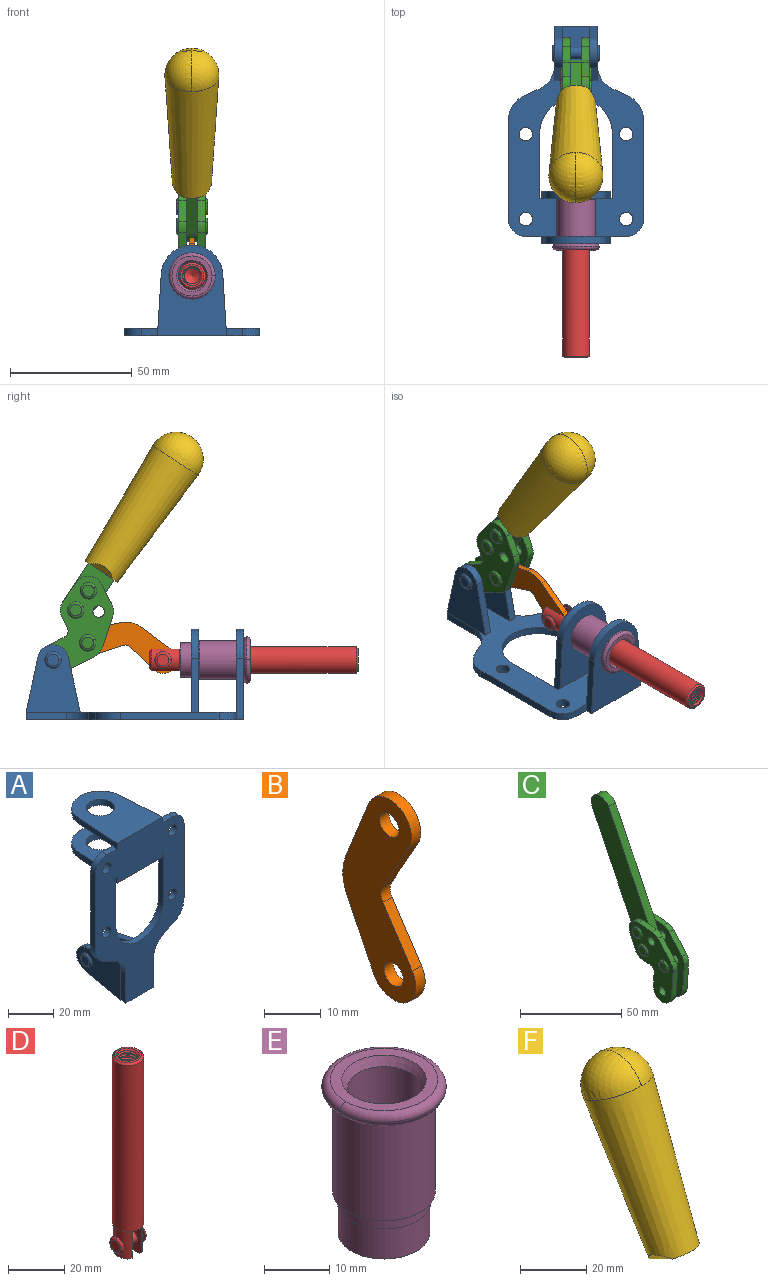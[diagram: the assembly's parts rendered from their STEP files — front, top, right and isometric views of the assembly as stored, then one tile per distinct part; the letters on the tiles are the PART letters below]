
ASSEMBLY  parts=6 mates=6
PART A: 55 faces, bbox 55.7x37.4x89.8 mm
  f0: torus R=2.41mm, axis (-1,0,0), area 15mm2, adj f11,f15,f25
  f1: torus R=2.41mm, axis (-1,0,0), area 15mm2, adj f10,f12,f22
  f2: cylinder r=2.78mm len=5.56mm, axis (0,-1,0), area 54.2mm2, adj f30,f54
  f3: cylinder r=14.99mm len=29.97mm, axis (0,-1,0), area 145.9mm2, adj f30,f49,f53,f54
  f4: cylinder r=2.78mm len=5.56mm, axis (0,-1,0), area 54.2mm2, adj f30,f54
  f5: cylinder r=2.78mm len=5.56mm, axis (0,-1,0), area 54.2mm2, adj f30,f54
  f6: cylinder r=2.78mm len=5.56mm, axis (0,-1,0), area 54.2mm2, adj f30,f54
  f7: cylinder r=6.35mm len=12.7mm, axis (0,0,1), area 123.6mm2, adj f27,f51
  f8: cylinder r=6.35mm len=12.7mm, axis (0,0,-1), area 124.7mm2, adj f21,f35
  f9: cylinder r=2.41mm len=11.18mm, axis (-1,0,0), area 169.4mm2, adj f16,f19
  f10: plane 4.83x4.83mm, normal (1,0,0), area 18.3mm2, adj f1,f12
  f11: plane 4.83x4.83mm, normal (-1,0,0), area 18.3mm2, adj f0,f15
  f12: torus R=2.41mm, axis (-1,0,0), area 15mm2, adj f1,f10,f22
  f13: cylinder r=6.35mm len=12.41mm, axis (1,0,0), area 53.4mm2, adj f18,f19,f22,f23
  f14: cylinder r=6.35mm len=12.41mm, axis (-1,0,0), area 53.4mm2, adj f16,f17,f24,f25
  f15: torus R=2.41mm, axis (-1,0,0), area 15mm2, adj f0,f11,f25
  f16: plane 27.86x22.35mm, normal (1,0,0), area 425.4mm2, adj f9,f14,f17,f24,f30
  f17: plane 22.86x4.97mm, normal (0,0.21,0.98), area 72.5mm2, adj f14,f16,f25,f30
  f18: plane 22.86x4.97mm, normal (0,0.21,0.98), area 72.5mm2, adj f13,f19,f22,f30
  f19: plane 27.86x22.35mm, normal (-1,0,0), area 425.4mm2, adj f9,f13,f18,f23,f30
  f20: cylinder r=12.7mm len=25.35mm, axis (0,0,-1), area 119.8mm2, adj f21,f34,f35,f36
  f21: plane 34.21x28.07mm, normal (0,0,-1), area 702.4mm2, adj f8,f20,f30,f34,f36
  f22: plane 27.96x22.45mm, normal (1,0,0), area 407.2mm2, adj f1,f12,f13,f18,f23,f30,f42,f43
  f23: plane 22.86x4.97mm, normal (0,0.21,-0.98), area 72.5mm2, adj f13,f19,f22,f44
  f24: plane 22.86x4.97mm, normal (0,0.21,-0.98), area 72.5mm2, adj f14,f16,f25,f44
  f25: plane 27.86x22.35mm, normal (-1,0,0), area 407.1mm2, adj f0,f14,f15,f17,f24,f30,f45,f46
  f26: plane 3.1x0.95mm, normal (0,0,-1), area 2.7mm2, adj f30,f49,f50,f54
  f27: plane 34.21x28.07mm, normal (0,0,1), area 702.4mm2, adj f7,f28,f30,f50,f52
  f28: cylinder r=12.7mm len=25.35mm, axis (0,0,1), area 118.8mm2, adj f27,f50,f51,f52
  f29: plane 3.1x0.95mm, normal (0,0,-1), area 2.7mm2, adj f30,f52,f53,f54
  f30: plane 86.54x55.63mm, normal (0,1,0), area 2362.9mm2, adj f2,f3,f4,f5,f6,f16,f17,f18
  f31: plane 40.56x3.1mm, normal (-1,0,0), area 125.7mm2, adj f30,f32,f48,f54
  f32: cylinder r=7.11mm len=7.11mm, axis (0,-1,0), area 34.6mm2, adj f30,f31,f33,f54
  f33: plane 6.67x3.1mm, normal (0,0,1), area 20.4mm2, adj f30,f32,f34,f54
  f34: plane 25.39x3.13mm, normal (-1,0.06,0), area 79.5mm2, adj f20,f21,f33,f35,f54
  f35: plane 37.31x28.45mm, normal (0,0,1), area 789.9mm2, adj f8,f20,f34,f36,f54
  f36: plane 25.39x3.13mm, normal (1,0.06,0), area 79.5mm2, adj f20,f21,f35,f37,f54
  f37: plane 6.67x3.1mm, normal (0,0,1), area 20.4mm2, adj f30,f36,f38,f54
  f38: cylinder r=7.11mm len=7.11mm, axis (0,-1,0), area 34.6mm2, adj f30,f37,f39,f54
  f39: plane 40.56x3.1mm, normal (1,0,0), area 125.7mm2, adj f30,f38,f40,f54
  f40: cylinder r=11.18mm len=10.16mm, axis (0,-1,0), area 39.5mm2, adj f30,f39,f41,f54
  f41: plane 6.09x3.1mm, normal (0.42,0,-0.91), area 20.8mm2, adj f30,f40,f42,f54
  f42: cylinder r=11.18mm len=9.41mm, axis (0,-1,0), area 37.2mm2, adj f22,f30,f41,f43,f54
  f43: plane 16.5x3.1mm, normal (1,0,0), area 51.1mm2, adj f22,f42,f44,f54
  f44: plane 17.37x3.1mm, normal (0,0,-1), area 53.8mm2, adj f23,f24,f30,f43,f45,f54
  f45: plane 16.5x3.1mm, normal (-1,0,0), area 51.1mm2, adj f25,f44,f46,f54
  f46: cylinder r=11.18mm len=9.41mm, axis (0,-1,0), area 37.2mm2, adj f25,f30,f45,f47,f54
  f47: plane 6.09x3.1mm, normal (-0.42,0,-0.91), area 20.8mm2, adj f30,f46,f48,f54
  f48: cylinder r=11.18mm len=10.16mm, axis (0,-1,0), area 39.5mm2, adj f30,f31,f47,f54
  f49: plane 26.54x3.1mm, normal (-1,0,0), area 82.3mm2, adj f3,f26,f30,f54
  f50: plane 25.39x3.1mm, normal (1,0.06,0), area 78.8mm2, adj f26,f27,f28,f51,f54
  f51: plane 37.31x28.45mm, normal (0,0,-1), area 789.9mm2, adj f7,f28,f50,f52,f54
  f52: plane 25.39x3.1mm, normal (-1,0.06,0), area 78.8mm2, adj f27,f28,f29,f51,f54
  f53: plane 26.54x3.1mm, normal (1,0,0), area 82.3mm2, adj f3,f29,f30,f54
  f54: plane 89.66x55.63mm, normal (0,-1,0), area 2678.5mm2, adj f2,f3,f4,f5,f6,f26,f29,f31
PART B: 12 faces, bbox 2.3x18.2x42.8 mm
  f0: cylinder r=2.4mm len=4.8mm, axis (1,0,0), area 34.9mm2, adj f4,f11
  f1: cylinder r=10.41mm len=8.47mm, axis (1,0,0), area 20.2mm2, adj f4,f9,f10,f11
  f2: cylinder r=3.05mm len=3.16mm, axis (1,0,0), area 7.7mm2, adj f4,f6,f7,f11
  f3: cylinder r=2.4mm len=4.8mm, axis (1,0,0), area 34.9mm2, adj f4,f11
  f4: plane 42.81x18.23mm, normal (-1,0,0), area 414.1mm2, adj f0,f1,f2,f3,f5,f6,f7,f8
  f5: cylinder r=5.54mm len=10.67mm, axis (1,0,0), area 41.8mm2, adj f4,f6,f10,f11
  f6: plane 11.66x6.53mm, normal (0,-0.87,-0.49), area 30.9mm2, adj f2,f4,f5,f11
  f7: plane 11.17x7.33mm, normal (0,-0.84,0.55), area 30.9mm2, adj f2,f4,f8,f11
  f8: cylinder r=5.54mm len=10.51mm, axis (1,0,0), area 41.8mm2, adj f4,f7,f9,f11
  f9: plane 13.67x6.67mm, normal (0,0.9,-0.44), area 35.1mm2, adj f1,f4,f8,f11
  f10: plane 14.1x5.7mm, normal (0,0.93,0.37), area 35.1mm2, adj f1,f4,f5,f11
  f11: plane 42.81x18.23mm, normal (1,0,0), area 414.1mm2, adj f0,f1,f2,f3,f5,f6,f7,f8
PART C: 59 faces, bbox 12.9x60.2x99.6 mm
  f0: torus R=2.39mm, axis (-1,0,0), area 14.9mm2, adj f20,f43,f51
  f1: torus R=2.39mm, axis (-1,0,0), area 14.9mm2, adj f19,f42,f51
  f2: torus R=2.39mm, axis (-1,0,0), area 14.9mm2, adj f18,f35,f51
  f3: torus R=2.39mm, axis (-1,0,0), area 14.9mm2, adj f14,f17,f23
  f4: torus R=2.39mm, axis (-1,0,0), area 14.9mm2, adj f13,f16,f23
  f5: torus R=2.39mm, axis (-1,0,0), area 14.9mm2, adj f12,f15,f23
  f6: cylinder r=2.39mm len=4.78mm, axis (1,0,0), area 46.5mm2, adj f48,f50,f51
  f7: cylinder r=2.39mm len=4.78mm, axis (1,0,0), area 46.5mm2, adj f50,f51
  f8: cylinder r=6.35mm len=12.68mm, axis (1,0,0), area 61.8mm2, adj f38,f39,f50,f51
  f9: cylinder r=2.39mm len=4.78mm, axis (-1,0,0), area 70.5mm2, adj f46,f50
  f10: cylinder r=2.39mm len=4.78mm, axis (-1,0,0), area 46.5mm2, adj f23,f45,f46
  f11: cylinder r=2.39mm len=4.78mm, axis (-1,0,0), area 46.5mm2, adj f23,f46
  f12: plane 4.78x4.78mm, normal (1,0,0), area 17.9mm2, adj f5,f15
  f13: plane 4.78x4.78mm, normal (1,0,0), area 17.9mm2, adj f4,f16
  f14: plane 4.78x4.78mm, normal (1,0,0), area 17.9mm2, adj f3,f17
  f15: torus R=2.39mm, axis (-1,0,0), area 14.9mm2, adj f5,f12,f23
  f16: torus R=2.39mm, axis (-1,0,0), area 14.9mm2, adj f4,f13,f23
  f17: torus R=2.39mm, axis (-1,0,0), area 14.9mm2, adj f3,f14,f23
  f18: plane 4.78x4.78mm, normal (-1,0,0), area 17.9mm2, adj f2,f35
  f19: plane 4.78x4.78mm, normal (-1,0,0), area 17.9mm2, adj f1,f42
  f20: plane 4.78x4.78mm, normal (-1,0,0), area 17.9mm2, adj f0,f43
  f21: plane 2.26x0.2mm, normal (1,0,0), area 0.2mm2, adj f31,f44
  f22: plane 2.26x0.2mm, normal (-1,0,0), area 0.2mm2, adj f41,f44
  f23: plane 39.37x30.77mm, normal (1,0,0), area 565.5mm2, adj f3,f4,f5,f10,f11,f15,f16,f17
  f24: cylinder r=6.1mm len=4.15mm, axis (-1,0,0), area 14.7mm2, adj f23,f25,f32,f46
  f25: plane 10.25x9.01mm, normal (0,-0.75,0.66), area 42.3mm2, adj f23,f24,f26,f46
  f26: cylinder r=6.35mm len=4.64mm, axis (-1,0,0), area 15.6mm2, adj f23,f25,f27,f46
  f27: plane 15.84x3.1mm, normal (0,-1,-0.07), area 49.2mm2, adj f23,f26,f28,f46
  f28: cylinder r=6.35mm len=12.68mm, axis (-1,0,0), area 61.8mm2, adj f23,f27,f29,f46
  f29: plane 8.11x3.1mm, normal (0,1,0.07), area 25.2mm2, adj f23,f28,f30,f46
  f30: cylinder r=3.05mm len=3.25mm, axis (-1,0,0), area 14.8mm2, adj f23,f29,f31,f46
  f31: plane 5.99x3.1mm, normal (0,0.07,-1), area 18.6mm2, adj f21,f23,f30,f44,f46
  f32: plane 9.5x3.1mm, normal (0,-0.07,1), area 29.5mm2, adj f23,f24,f33,f46,f47
  f33: cylinder r=6.1mm len=8.63mm, axis (-1,0,0), area 39.1mm2, adj f23,f32,f34,f47
  f34: plane 8.65x3.96mm, normal (0,0.91,-0.42), area 29.5mm2, adj f23,f33,f44,f47
  f35: torus R=2.39mm, axis (-1,0,0), area 14.9mm2, adj f2,f18,f51
  f36: plane 10.25x9.01mm, normal (0,-0.75,0.66), area 42.3mm2, adj f37,f49,f50,f51
  f37: cylinder r=6.35mm len=4.64mm, axis (1,0,0), area 15.6mm2, adj f36,f38,f50,f51
  f38: plane 15.84x3.1mm, normal (0,-1,-0.07), area 49.2mm2, adj f8,f37,f50,f51
  f39: plane 8.11x3.1mm, normal (0,1,0.07), area 25.2mm2, adj f8,f40,f50,f51
  f40: cylinder r=3.05mm len=3.25mm, axis (1,0,0), area 14.8mm2, adj f39,f41,f50,f51
  f41: plane 5.99x3.1mm, normal (0,0.07,-1), area 18.6mm2, adj f22,f40,f44,f50,f51
  f42: torus R=2.39mm, axis (-1,0,0), area 14.9mm2, adj f1,f19,f51
  f43: torus R=2.39mm, axis (-1,0,0), area 14.9mm2, adj f0,f20,f51
  f44: cylinder r=6.35mm len=12.12mm, axis (-1,0,0), area 128.9mm2, adj f21,f22,f23,f31,f34,f41,f46,f47
  f45: plane 2.65x1.35mm, normal (1,0,0), area 1mm2, adj f10,f55
  f46: plane 39.08x20.42mm, normal (-1,0,0), area 412.5mm2, adj f9,f10,f11,f24,f25,f26,f27,f28
  f47: plane 77.62x39.82mm, normal (1,0,0), area 850mm2, adj f32,f33,f34,f44,f53,f54,f55
  f48: plane 2.65x1.35mm, normal (-1,0,0), area 1mm2, adj f6,f55
  f49: cylinder r=6.1mm len=4.15mm, axis (1,0,0), area 14.7mm2, adj f36,f50,f51,f56
  f50: plane 39.08x20.42mm, normal (1,0,0), area 412.5mm2, adj f6,f7,f8,f9,f36,f37,f38,f39
  f51: plane 39.37x30.77mm, normal (-1,0,0), area 565.5mm2, adj f0,f1,f2,f6,f7,f8,f35,f36
  f52: plane 8.65x3.96mm, normal (0,0.91,-0.42), area 29.5mm2, adj f44,f51,f57,f58
  f53: plane 68.49x33.4mm, normal (0,0.9,-0.44), area 358.1mm2, adj f44,f47,f54,f58
  f54: cylinder r=6.35mm len=12.06mm, axis (1,0,0), area 93.7mm2, adj f47,f53,f55,f58
  f55: plane 68.49x33.4mm, normal (0,-0.9,0.44), area 358.1mm2, adj f44,f45,f46,f47,f48,f50,f54,f58
  f56: plane 9.5x3.1mm, normal (0,-0.07,1), area 29.5mm2, adj f49,f50,f51,f57,f58
  f57: cylinder r=6.1mm len=8.63mm, axis (1,0,0), area 39.1mm2, adj f51,f52,f56,f58
  f58: plane 77.62x39.82mm, normal (-1,0,0), area 850mm2, adj f44,f52,f53,f54,f55,f56,f57
PART D: 48 faces, bbox 12.6x11.1x86.1 mm
  f0: torus R=2.41mm, axis (-1,0,0), area 15mm2, adj f30,f32,f34
  f1: torus R=2.41mm, axis (-1,0,0), area 15mm2, adj f29,f31,f33
  f2: cylinder r=5.54mm len=72.39mm, axis (0,0,1), area 2518.5mm2, adj f3,f4,f42,f43
  f3: cone r=5.54mm half-angle=45deg, axis (0,0,1), area 7.6mm2, adj f2,f5,f41
  f4: cone r=5.54mm half-angle=45deg, axis (0,0,-1), area 34.9mm2, adj f2,f39
  f5: cylinder r=5.08mm len=11.48mm, axis (0,0,1), area 108.3mm2, adj f3,f7,f8,f41
  f6: cylinder r=2.41mm len=4.83mm, axis (-1,0,0), area 71.2mm2, adj f40,f41
  f7: cylinder r=2.41mm len=4.83mm, axis (-1,0,0), area 7.6mm2, adj f5,f34
  f8: cone r=5.08mm half-angle=45deg, axis (0,0,1), area 10.6mm2, adj f5,f37,f41
  f9: cone r=3.98mm half-angle=45deg, axis (0,0,1), area 17.6mm2, adj f27,f39,f45,f46,f47
  f10: cylinder r=2.41mm len=4.83mm, axis (-1,0,0), area 7.6mm2, adj f33,f38
  f11: cylinder r=3.2mm len=6.4mm, axis (0,0,1), area 78.4mm2, adj f12,f28,f44,f45,f47
  f12: cylinder r=3.2mm len=6.4mm, axis (0,0,1), area 10.5mm2, adj f11,f13,f45,f47
  f13: cylinder r=3.2mm len=6.4mm, axis (0,0,1), area 10.5mm2, adj f12,f14,f45,f47
  f14: cylinder r=3.2mm len=6.4mm, axis (0,0,1), area 10.5mm2, adj f13,f15,f45,f47
  f15: cylinder r=3.2mm len=6.4mm, axis (0,0,1), area 10.5mm2, adj f14,f16,f45,f47
  f16: cylinder r=3.2mm len=6.4mm, axis (0,0,1), area 10.5mm2, adj f15,f17,f45,f47
  f17: cylinder r=3.2mm len=6.4mm, axis (0,0,1), area 10.5mm2, adj f16,f18,f45,f47
  f18: cylinder r=3.2mm len=6.4mm, axis (0,0,1), area 10.5mm2, adj f17,f19,f45,f47
  f19: cylinder r=3.2mm len=6.4mm, axis (0,0,1), area 10.5mm2, adj f18,f20,f45,f47
  f20: cylinder r=3.2mm len=6.4mm, axis (0,0,1), area 10.5mm2, adj f19,f21,f45,f47
  f21: cylinder r=3.2mm len=6.4mm, axis (0,0,1), area 10.5mm2, adj f20,f22,f45,f47
  f22: cylinder r=3.2mm len=6.4mm, axis (0,0,1), area 10.5mm2, adj f21,f23,f45,f47
  f23: cylinder r=3.2mm len=6.4mm, axis (0,0,1), area 10.5mm2, adj f22,f24,f45,f47
  f24: cylinder r=3.2mm len=6.4mm, axis (0,0,1), area 10.5mm2, adj f23,f25,f45,f47
  f25: cylinder r=3.2mm len=6.4mm, axis (0,0,1), area 10.5mm2, adj f24,f26,f45,f47
  f26: cylinder r=3.2mm len=6.4mm, axis (0,0,1), area 10.5mm2, adj f25,f27,f45,f47
  f27: cylinder r=3.2mm len=6.4mm, axis (0,0,1), area 7.4mm2, adj f9,f26,f45,f47
  f28: cone r=3.2mm half-angle=60deg, axis (0,0,1), area 37.2mm2, adj f11
  f29: plane 4.83x4.83mm, normal (-1,0,0), area 18.3mm2, adj f1,f31
  f30: plane 4.83x4.83mm, normal (1,0,0), area 18.3mm2, adj f0,f32
  f31: torus R=2.41mm, axis (-1,0,0), area 15mm2, adj f1,f29,f33
  f32: torus R=2.41mm, axis (-1,0,0), area 15mm2, adj f0,f30,f34
  f33: plane 6.83x6.83mm, normal (1,0,0), area 18.3mm2, adj f1,f10,f31
  f34: plane 6.83x6.83mm, normal (-1,0,0), area 18.3mm2, adj f0,f7,f32
  f35: cone r=5.08mm half-angle=45deg, axis (0,0,1), area 10.6mm2, adj f36,f38,f40
  f36: plane 7.25x1.97mm, normal (0,0,-1), area 10mm2, adj f35,f40
  f37: plane 7.25x1.97mm, normal (0,0,-1), area 10mm2, adj f8,f41
  f38: cylinder r=5.08mm len=11.48mm, axis (0,0,1), area 108.3mm2, adj f10,f35,f40,f42
  f39: plane 9.55x9.55mm, normal (0,0,1), area 22mm2, adj f4,f9
  f40: plane 12.76x10.09mm, normal (1,0,0), area 95.7mm2, adj f6,f35,f36,f38,f42,f43
  f41: plane 12.76x10.09mm, normal (-1,0,0), area 95.7mm2, adj f3,f5,f6,f8,f37,f43
  f42: cone r=5.54mm half-angle=45deg, axis (0,0,1), area 7.6mm2, adj f2,f38,f40
  f43: plane 11.07x4.7mm, normal (0,0,-1), area 50.4mm2, adj f2,f40,f41
  f44: plane 0.89x0.62mm, normal (-1,0,0), area 0.3mm2, adj f11,f45,f46,f47
  f45: bspline ~24.8x7.63mm, area 266.6mm2, adj f9,f11,f12,f13,f14,f15,f16,f17
  f46: bspline ~24.87x7.63mm, area 73.6mm2, adj f9,f44,f45,f47
  f47: bspline ~24.98x7.63mm, area 272.5mm2, adj f9,f11,f12,f13,f14,f15,f16,f17
PART E: 15 faces, bbox 20.6x20.6x28.7 mm
  f0: torus R=8.26mm, axis (0,0,1), area 56.8mm2, adj f1,f10,f12
  f1: torus R=8.26mm, axis (0,0,1), area 56.8mm2, adj f0,f6,f13
  f2: cylinder r=5.59mm len=25.91mm, axis (0,0,1), area 909.6mm2, adj f3,f4
  f3: cone r=6.86mm half-angle=45deg, axis (0,0,-1), area 70.2mm2, adj f2,f14
  f4: cone r=6.47mm half-angle=30deg, axis (0,0,1), area 66.7mm2, adj f2,f13
  f5: cylinder r=7.04mm len=14.07mm, axis (0,0,1), area 252.6mm2, adj f11,f14
  f6: torus R=8.26mm, axis (0,0,1), area 56.8mm2, adj f1,f12,f13
  f7: cylinder r=7.16mm len=14.33mm, axis (0,0,1), area 91.5mm2, adj f9,f11
  f8: cylinder r=7.86mm len=18.42mm, axis (0,0,1), area 909.6mm2, adj f9,f10
  f9: plane 15.72x15.72mm, normal (0,0,-1), area 33mm2, adj f7,f8
  f10: plane 16.51x16.51mm, normal (0,0,-1), area 19.9mm2, adj f0,f8,f12
  f11: plane 14.33x14.33mm, normal (0,0,-1), area 5.7mm2, adj f5,f7
  f12: torus R=8.26mm, axis (0,0,1), area 56.8mm2, adj f0,f6,f10
  f13: plane 16.51x16.51mm, normal (0,0,1), area 82.7mm2, adj f1,f4,f6
  f14: plane 14.07x14.07mm, normal (0,0,-1), area 7.8mm2, adj f3,f5
PART F: 11 faces, bbox 22.3x42.6x64.5 mm
  f0: sphere r=11.13mm, area 411.4mm2, adj f1,f8
  f1: cone r=11.11mm half-angle=3.3deg, axis (0,0.44,0.9), area 3251.8mm2, adj f0,f7,f8,f9,f10
  f2: cylinder r=6.16mm len=11.7mm, axis (1,0,0), area 89.5mm2, adj f3,f4,f5,f6
  f3: plane 60.23x36.75mm, normal (-1,0,0), area 763.6mm2, adj f2,f4,f6,f10
  f4: plane 51.37x25.05mm, normal (0,0.9,-0.44), area 264.2mm2, adj f2,f3,f5,f10
  f5: plane 60.23x36.75mm, normal (1,0,0), area 763.6mm2, adj f2,f4,f6,f10
  f6: plane 51.37x25.05mm, normal (0,-0.9,0.44), area 264.2mm2, adj f2,f3,f5,f10
  f7: plane 9.95x5.95mm, normal (0.71,-0.31,-0.64), area 25.8mm2, adj f1,f10
  f8: sphere r=11.13mm, area 411.4mm2, adj f0,f1
  f9: plane 9.95x5.95mm, normal (-0.71,-0.31,-0.64), area 25.8mm2, adj f1,f10
  f10: plane 14.27x11.38mm, normal (0,-0.44,-0.9), area 106.7mm2, adj f1,f3,f4,f5,f6,f7,f9
PLACE A rot(axis=(1,0,0),90deg) t=(0,0,0)mm fixed
PLACE B rot(axis=(1,0,0),104.8deg) t=(0,8.16,4.78)mm
PLACE C rot(axis=(1,0,0),59.7deg) t=(0,-8.04,19.59)mm
PLACE D rot(axis=(1,0,0),90deg) t=(0,2.38,0)mm
PLACE E rot(axis=(1,0,0),90deg) t=(0,0,0)mm
PLACE F rot(axis=(1,0,0),59.7deg) t=(-0.04,-8.04,19.59)mm
MATE fastened F.f2 <-> C.f54  axis (1,0,0) through (-2.35,-19.42,108.57)mm
MATE slider D.f2 <-> E.f2  axis (0,-1,0) through (0,-56.4,24.61)mm
MATE revolute B.f5 <-> D.f6  axis (1,0,0) through (0,-13.09,24.61)mm
MATE revolute B.f3 <-> C.f4  axis (1,0,0) through (0,17.87,31.66)mm
MATE fastened E.f0 <-> A.f7  axis (0,1,0) through (0,-46.39,24.61)mm
MATE revolute C.f7 <-> A.f0  axis (-1,0,0) through (0,32.09,24.61)mm
